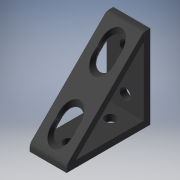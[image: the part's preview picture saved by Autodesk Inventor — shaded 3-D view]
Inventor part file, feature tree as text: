
AUTODESK INVENTOR PART (.ipt)
format: ipt  version: 2019 (Build 230136000, 136)  size: 173,568 bytes
history: native  units: mm
features: sketch x9, extrude x5, hole x4
ambient origin geometry x8: Origin, YZ Plane, XZ Plane, XY Plane, X Axis, Y Axis, Z Axis, Center Point
bodies: Solid1 (feature_tree)
feature tree (18):
  extrude  "Extrusion1"  Depth=46.0mm TaperAngle=0.0deg
  hole  "Hole1"  [1 undecoded]
  hole  "Hole2"  [1 undecoded]
  extrude  "Extrusion2"  [1 undecoded]
  extrude  "Extrusion3"  [1 undecoded]
  hole  "Hole3"  [1 undecoded]
  hole  "Hole4"  [1 undecoded]
  extrude  "Extrusion4"  [1 undecoded]
  extrude  "Extrusion5"  [1 undecoded]
  sketch  "Sketch_1"  dims[d0=22.0mm d1=0.0mm]
  sketch  "Sketch2"  dims[d2=6.81mm d3=6.0mm d4=4.0mm d5=2.0mm d6=90.0deg d7=4.0mm d8=0.0mm]
  sketch  "Sketch3"  dims[d9=6.81mm d10=6.0mm d11=4.0mm d12=2.0mm d13=90.0deg d14=4.0mm d15=0.0mm d16=46.0mm d17=0.0mm]
  sketch  "Sketch_4"  dims[d18=46.0mm d19=0.0mm]
  sketch  "Sketch_5"  dims[d20=6.81mm d21=6.0mm d22=4.0mm d23=2.0mm d24=90.0deg d25=4.0mm d26=0.0mm]
  sketch  "Sketch6"  dims[d27=6.81mm d28=6.0mm d29=4.0mm d30=2.0mm d31=90.0deg d32=4.0mm d33=0.0mm d34=46.0mm d35=0.0mm]
  sketch  "Sketch7"  dims[d36=46.0mm d37=0.0mm]
  sketch  "Sketch_8"
  sketch  "Sketch_9"
note: 8 required parameter values undecoded (feature->parameter linkage not recoverable at this tier; creation-order binding heuristic only, values carry confidence <= 0.55)
